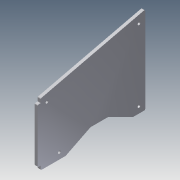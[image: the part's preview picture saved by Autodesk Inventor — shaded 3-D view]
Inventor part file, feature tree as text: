
AUTODESK INVENTOR PART (.ipt)
format: ipt  version: 2014 (Build 180170000, 170)  size: 150,528 bytes
history: native  units: mm
features: extrude x5, sketch x5, fillet x1
ambient origin geometry x8: Origin, YZ Plane, XZ Plane, XY Plane, X Axis, Y Axis, Z Axis, Center Point
bodies: Solid1 (feature_tree)
feature tree (11):
  extrude  "Extrusion1"  Depth=210.0mm
  extrude  "Extrusion2"  Depth=25.0mm
  extrude  "Extrusion3"  Depth=6.0mm TaperAngle=0.0deg
  extrude  "Extrusion4"  Depth=3.0mm TaperAngle=0.0deg
  extrude  "Extrusion5"  Depth=8.1mm
  fillet  "Fillet1"  Radius=6.0mm
  sketch  "Sketch1"  dims[d0=150.0mm d1=210.0mm]
  sketch  "Sketch2"  dims[d2=6.0mm d3=0.0mm d4=25.0mm]
  sketch  "Sketch3"  dims[d5=50.0mm d6=6.0mm d7=0.0mm]
  sketch  "Sketch4"  dims[d8=50.0mm d9=3.0mm d10=0.0mm]
  sketch  "Sketch5"  dims[d11=8.1mm d12=8.1mm d13=6.0mm d14=6.0mm d15=0.0mm d16=2.0mm d17=12.5mm d18=12.5mm d19=12.5mm d21=5.4mm d22=37.5mm d23=6.0mm d24=0.0mm d25=50.0mm d26=12.5mm]
